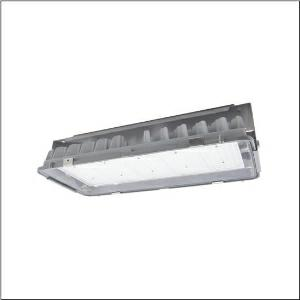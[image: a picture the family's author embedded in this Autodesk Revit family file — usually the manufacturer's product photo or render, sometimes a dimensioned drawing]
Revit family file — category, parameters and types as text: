
# Revit family: highbay_11xtreme_51hf61da4mma
name_source: partatom
category: Lighting Fixtures
units: mm (PartAtom-declared; Revit-internal decimal feet)

## family parameters
Cut with Voids When Loaded = No
Host = Face
Light Source = No
Part Type = Normal
Room Calculation Point = No
Round Connector Dimension = Use Diameter
Shared = No

## types (1)
- --- (1 x LED, 31500 lm, 170.8 W, 4000K)
    Apparent Load = 171 VA
    CIE Flux Codes = 88 96 99 100 100
    Color Rendering = 80
    Color Temperature = 4000K
    Default Elevation = 1800 mm
    Description = Highbay 11Xtreme, high bay luminaire, primary light control with lens, of PMMA, primary optical cover: cover, of toughened safety glass, light emission: direct distribution, primary light characteristic: symmetric, installation type: suspended mounting, surface-mounted, 1x LED module,for 1x LED, rated luminous flux: 31.500lm, luminous efficacy: 184lm/W, light colour: 840, colour temperature: 4000K, control gear: DALI 2, with cable H07RN-F 5x 1.5mm², mains connection: 220..240V, AC, 50/60Hz, cable length: 1,5m, rated input power: 171W, luminaire housing, of diecast aluminium, coated, silver, length: 595mm, width: 280mm, height: 195mm, protection rating (complete): IP66, insulation class (complete): insulation class I (protective earthing), certification: CE, ENEC, UKCA, protection symbol: D, ball protection: ball impact resistant according to DIN VDE 0710 part 13 (with chain suspension), impact resistance: IK08, permissible operating ambient temperature: -25..+60°C, reducing of maximum allowable ambient temperature of 5°C with ceiling mounting, packaging unit: 1 piece
    Height = 157 mm
    Lamp = 1 x LED
    Lamp Light Flux = 31500 lm
    Lamp Power = 170.8 W
    Lamp count = 1
    Length = 593 mm
    Luminous efficacy = 184 lm/W
    Manufacturer = Siteco
    ModVariant = No
    Model = 51HF61DA4MMA
    Mounting Place = Ceiling
    Mounting Type = Pendant
    Number of Poles = 1
    OnlyDefault = Yes
    Power Factor = 1
    Product Name = Highbay 11Xtreme
    Product group = high bay luminaire
    ProductGroupID = 901
    Protection Class = Protection class I
    Protection Degree = IP 66
    RLX_Detail_Level = 1
    RLX_Emergency_Light_Flux = 0 lm
    RLX_Emergency_Type = 0
    RLX_Emergency_Type_DB = No
    RlxData = <blob elided: 27905 chars, md5=97ca95a3>
    Socket = socket
    Standby Power = 0 W
    System Light Flux = 31501 lm
    System Power = 171 W
    Type Comments = factory setting: luminous flux: 100 % | dim-lin: 254 | 1132 mA
    Type Image = l_1258342.jpg
    URL = http://relux.com
    VarID = @adj_104963
    Voltage = 0 V
    Weight = 0.00 kg
    Width = 278 mm

## geometry (parser evidence)
native form markers: Blend x4, Sweep x11
no freeform markers — native parametric forms only
